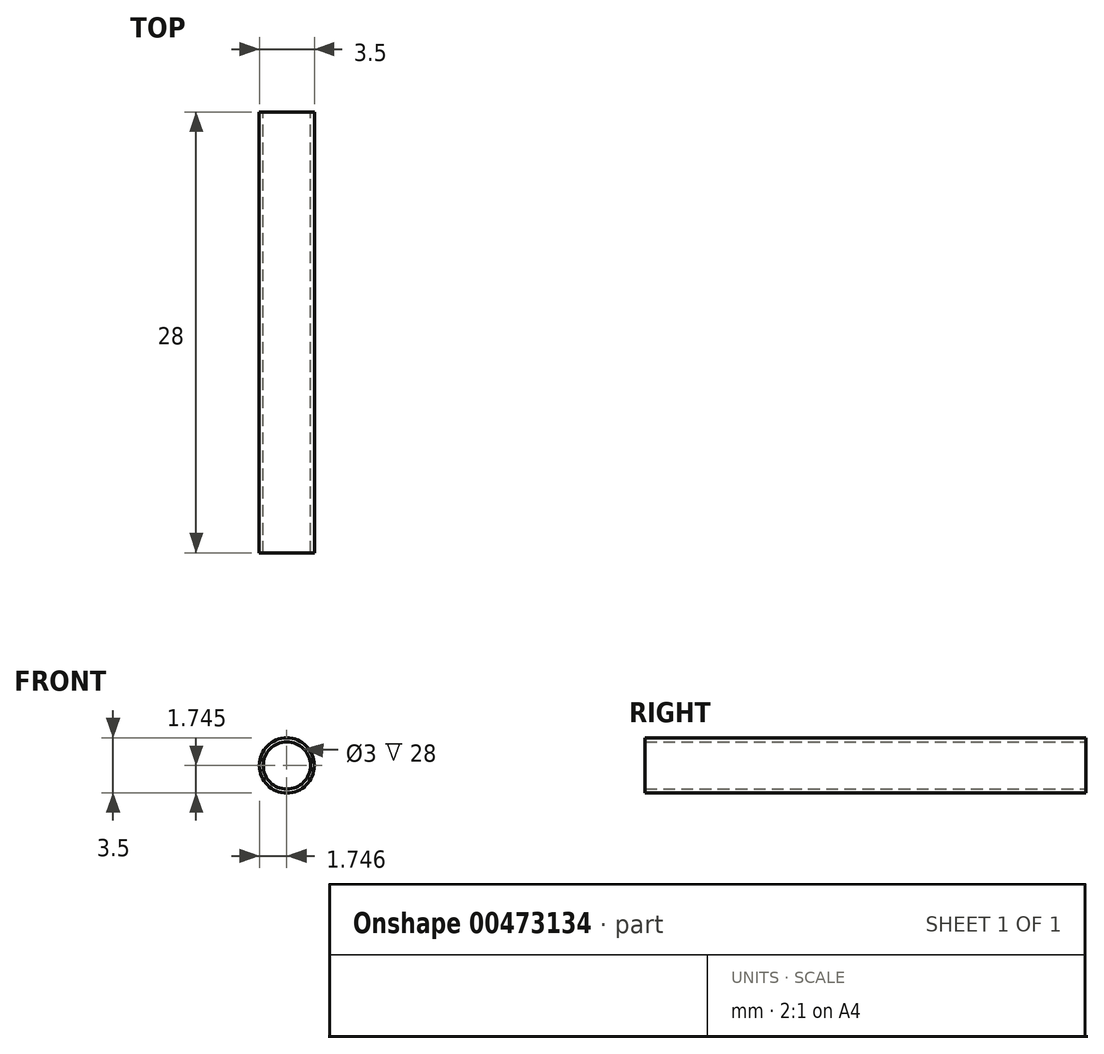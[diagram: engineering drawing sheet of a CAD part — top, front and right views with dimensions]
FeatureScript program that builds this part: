
annotation { "Feature Type Name" : "Feature", "Feature Type Description" : "" }
export const myFeature = defineFeature(function(context is Context, id is Id, definition is map)
    precondition{}
    {
        {
            var Q0;
            Q0=qCreatedBy(makeId("Front.planeOp"),FACE);
            var sketch = newSketch(context, id + "F0", { "sketchPlane" : qUnion([Q0])});
            skCircle(sketch, "E0", {"center": v(-50.65, 40) * mm, "radius": 1.5 * mm});
            skCircle(sketch, "E1", {"center": v(-50.65, 40) * mm, "radius": 1.75 * mm});
            skSolve(sketch);
        }
        {
            var Q0;
            Q0=makeQuery(id+"F0.imprint","IMPRINT",FACE,{"disambiguationData":[TD([[makeQuery(id+"F0.imprint","IMPRINT",EDGE,{"derivedFrom":sQuery(id+"F0.wireOp",EDGE,"E0")}),-1.0]])]});
            extrude(context, id + "F1", {"entities" : qUnion([Q0]), "depth" : 28 * mm});
        }
    });
